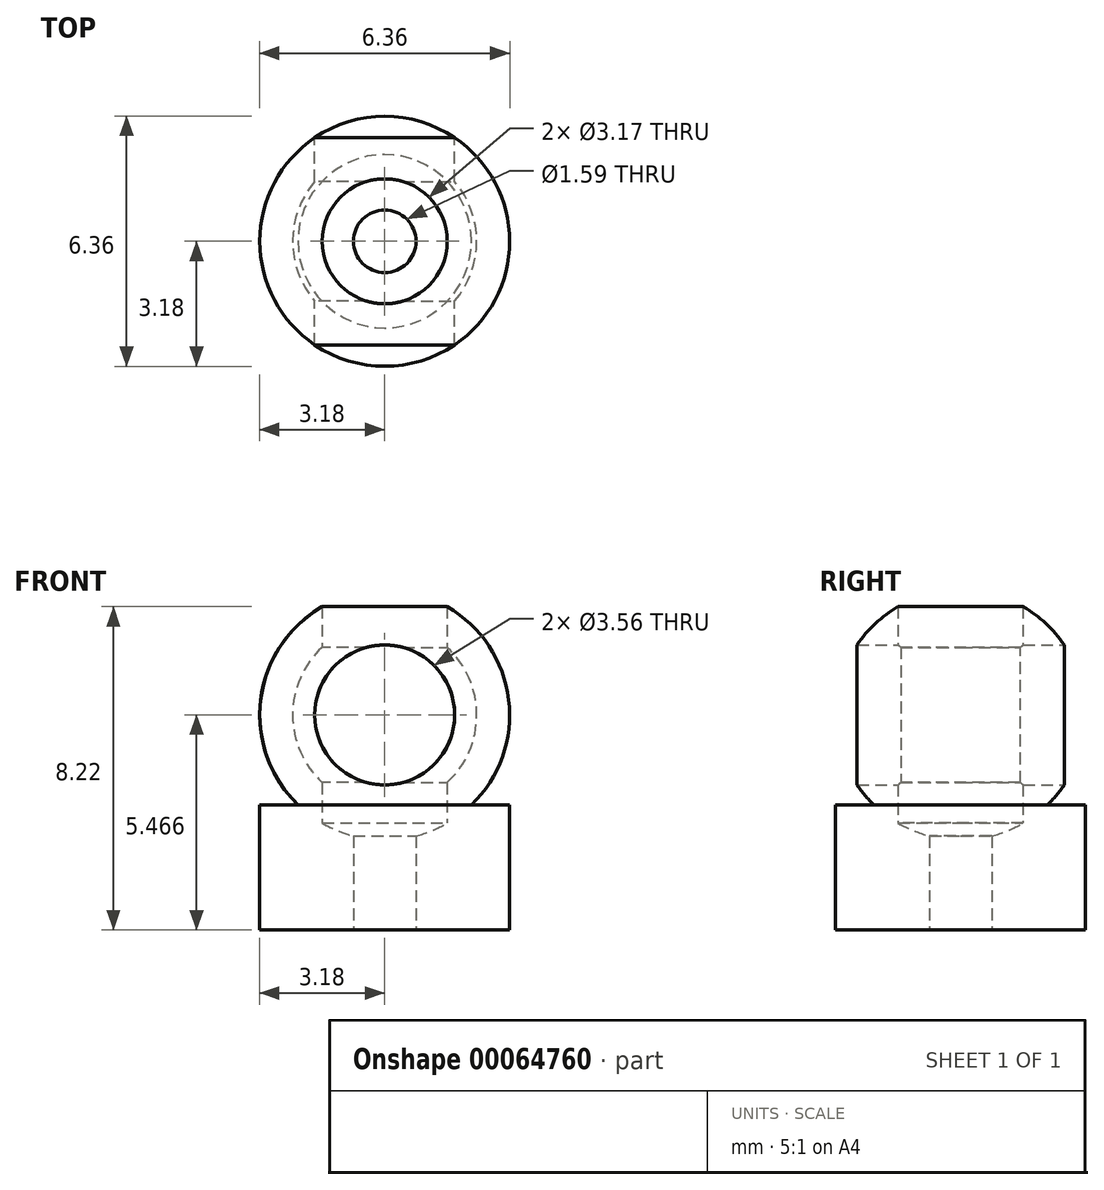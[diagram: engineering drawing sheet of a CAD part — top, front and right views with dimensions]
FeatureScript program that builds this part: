
annotation { "Feature Type Name" : "Feature", "Feature Type Description" : "" }
export const myFeature = defineFeature(function(context is Context, id is Id, definition is map)
    precondition{}
    {
        {
            var Q0;
            Q0=qCreatedBy(makeId("Front.planeOp"),FACE);
            var sketch = newSketch(context, id + "F0", { "sketchPlane" : qUnion([Q0])});
            skLineSegment(sketch, "E0.bottom", {"start": v(0, 0) * mm, "end": v(3.18, 0) * mm});
            skLineSegment(sketch, "E0.top", {"start": v(0, -3.18) * mm, "end": v(3.18, -3.18) * mm});
            skLineSegment(sketch, "E0.left", {"start": v(0, 0) * mm, "end": v(0, -3.17) * mm});
            skLineSegment(sketch, "E0.right", {"start": v(3.18, 0) * mm, "end": v(3.18, -3.17) * mm});
            skLineSegment(sketch, "E1", {"start": v(0.8, -3.18) * mm, "end": v(0.8, -0.89) * mm});
            skLineSegment(sketch, "E2", {"start": v(0.8, -0.89) * mm, "end": v(0.8, 2.29) * mm});
            skLineSegment(sketch, "E3", {"start": v(0.8, 2.29) * mm, "end": v(0, 2.29) * mm});
            skLineSegment(sketch, "E4", {"start": v(0.8, -0.89) * mm, "end": v(0, -0.89) * mm});
            skArc(sketch, "E5", {"start": v(0, -0.89) * mm, "mid": v(3.17, 2.29) * mm, "end": v(0, 5.46) * mm});
            skLineSegment(sketch, "E6", {"start": v(0, -0.89) * mm, "end": v(0, 5.46) * mm});
            skArc(sketch, "E7", {"start": v(0, -0.05) * mm, "mid": v(2.34, 2.29) * mm, "end": v(0, 4.62) * mm});
            skLineSegment(sketch, "E8", {"start": v(1.59, 2.27) * mm, "end": v(1.59, -0.46) * mm});
            skLineSegment(sketch, "E9", {"start": v(1.59, 2.27) * mm, "end": v(1.59, 5.04) * mm});
            skSolve(sketch);
        }
        {
            var Q0;
            {var subQ1=sQuery(id+"F0.wireOp",EDGE,"E5");var subQ5=sQuery(id+"F0.wireOp",EDGE,"E0.bottom");var subQ6=makeQuery(id+"F0.imprint","INTERSECT",VERTEX,{"derivedFrom":[subQ5,subQ1]});Q0=makeQuery(id+"F0.imprint","IMPRINT",FACE,{"disambiguationData":[TD([[makeQuery(id+"F0.imprint","IMPRINT",EDGE,{"disambiguationData":[TD([[subQ6,1.0]])],"derivedFrom":subQ5}),1.0]])]});}
            var Q1;
            {var subQ1=sQuery(id+"F0.wireOp",EDGE,"E0.right");Q1=makeQuery(id+"F0.imprint","IMPRINT",FACE,{"disambiguationData":[TD([[makeQuery(id+"F0.imprint","IMPRINT",EDGE,{"derivedFrom":subQ1}),-1.0]])]});}
            var Q2;
            {var subQ0=sQuery(id+"F0.wireOp",EDGE,"E5");var subQ1=sQuery(id+"F0.wireOp",EDGE,"E0.bottom");var subQ2=makeQuery(id+"F0.imprint","INTERSECT",VERTEX,{"derivedFrom":[subQ1,subQ0]});Q2=makeQuery(id+"F0.imprint","IMPRINT",FACE,{"disambiguationData":[TD([[makeQuery(id+"F0.imprint","IMPRINT",EDGE,{"disambiguationData":[TD([[subQ2,1.0]])],"derivedFrom":subQ1}),-1.0]])]});}
            var Q3;
            Q3=sQuery(id+"F0.wireOp",EDGE,"E6");
            revolve(context, id + "F1", {"entities" : qUnion([Q0, Q1, Q2]), "axis" : qUnion([Q3]), "revolveType" : RevolveType.FULL});
        }
        {
            var Q0;
            Q0=qCreatedBy(makeId("Front.planeOp"),FACE);
            var sketch = newSketch(context, id + "F2", { "sketchPlane" : qUnion([Q0])});
            skLineSegment(sketch, "E10", {"start": v(0, 0) * mm, "end": v(0, 0.5) * mm, "construction": true});
            skLineSegment(sketch, "E11", {"start": v(0, 0.5) * mm, "end": v(0, 2.29) * mm});
            skCircle(sketch, "E12", {"center": v(0, 2.29) * mm, "radius": 1.78 * mm});
            skSolve(sketch);
        }
        {
            var Q0;
            Q0=makeQuery(id+"F2.imprint","IMPRINT",FACE,{"disambiguationData":[TD([[makeQuery(id+"F2.imprint","IMPRINT",EDGE,{"derivedFrom":sQuery(id+"F2.wireOp",EDGE,"E12")}),1.0]])]});
            extrude(context, id + "F3", {"entities" : qUnion([Q0]), "operationType" : NewBodyOperationType.REMOVE, "endBound" : BoundingType.THROUGH_ALL, "depth" : 25.4 * mm, "hasSecondDirection" : true, "secondDirectionOppositeDirection" : true, "secondDirectionDepth" : 25.4 * mm});
        }
    });
